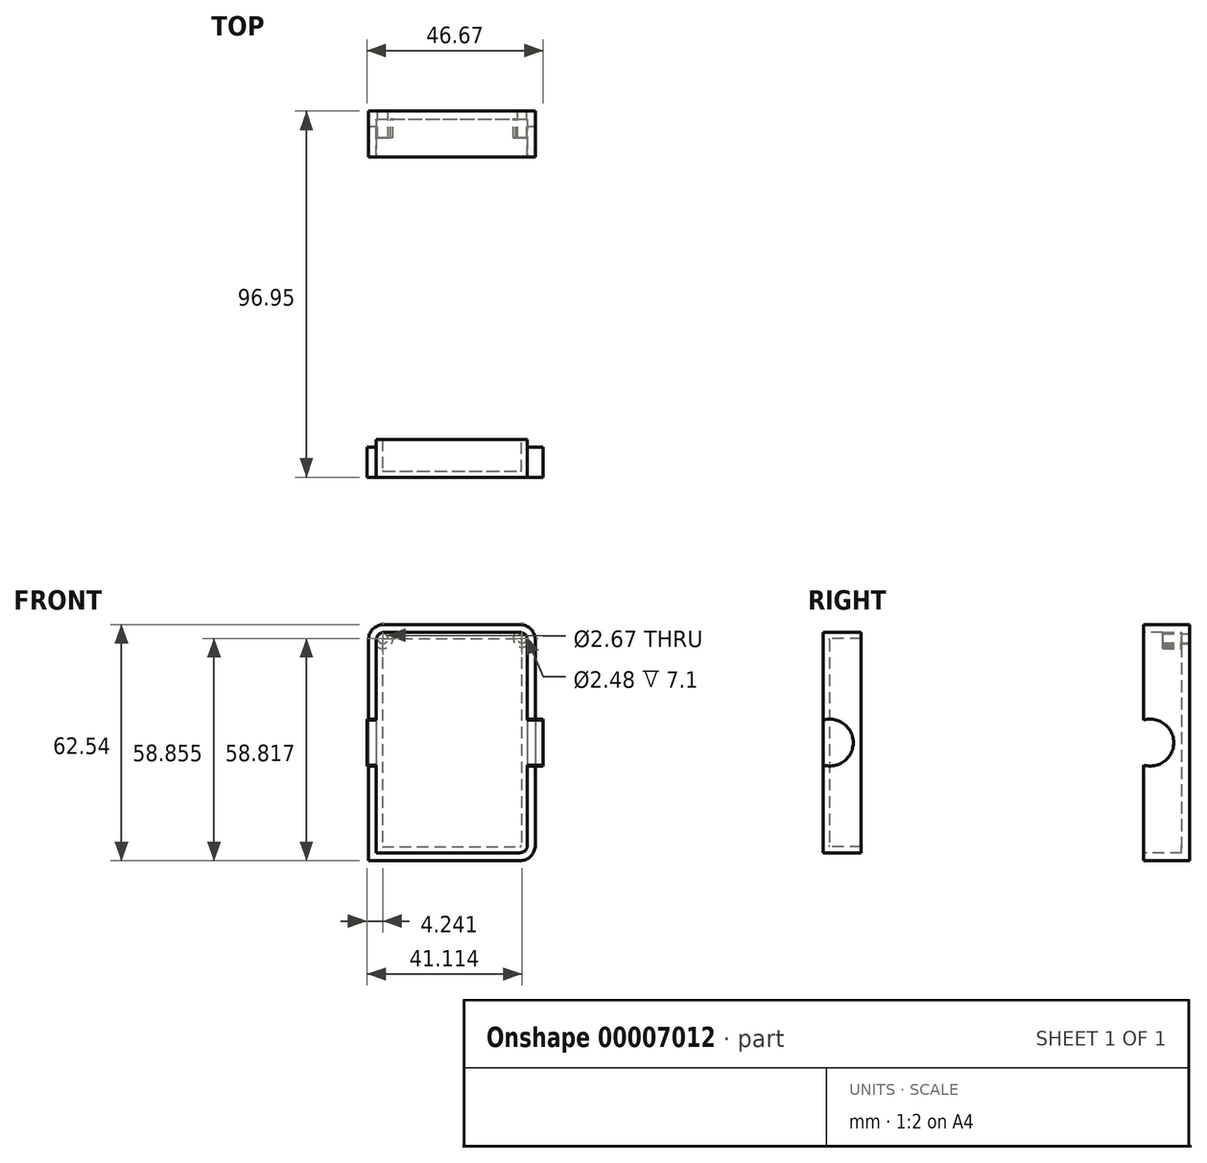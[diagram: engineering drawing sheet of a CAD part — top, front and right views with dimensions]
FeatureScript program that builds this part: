
annotation { "Feature Type Name" : "Feature", "Feature Type Description" : "" }
export const myFeature = defineFeature(function(context is Context, id is Id, definition is map)
    precondition{}
    {
        {
            var Q0;
            Q0=qCreatedBy(makeId("Front.planeOp"),FACE);
            var sketch = newSketch(context, id + "F0", { "sketchPlane" : qUnion([Q0])});
            skLineSegment(sketch, "E0.bottom", {"start": v(-18, 29.17) * mm, "end": v(18, 29.17) * mm});
            skLineSegment(sketch, "E0.top", {"start": v(-20, -29.17) * mm, "end": v(18, -29.17) * mm});
            skLineSegment(sketch, "E0.left", {"start": v(-20, 27.17) * mm, "end": v(-20, -29.17) * mm});
            skLineSegment(sketch, "E0.right", {"start": v(20, 27.17) * mm, "end": v(20, -27.17) * mm});
            skLineSegment(sketch, "E1", {"start": v(0, 39.19) * mm, "end": v(0, 29.17) * mm});
            skLineSegment(sketch, "E2", {"start": v(20, 0) * mm, "end": v(28.08, 0) * mm});
            skPoint(sketch, "E3.visualSharp", {"position": v(-20, 29.17) * mm});
            skArc(sketch, "E3.filletArc", {"start": v(-18, 29.17) * mm, "mid": v(-19.41, 28.58) * mm, "end": v(-20, 27.17) * mm});
            skPoint(sketch, "E4.visualSharp", {"position": v(20, 29.17) * mm});
            skArc(sketch, "E4.filletArc", {"start": v(20, 27.17) * mm, "mid": v(19.41, 28.58) * mm, "end": v(18, 29.17) * mm});
            skPoint(sketch, "E5.visualSharp", {"position": v(20, -29.17) * mm});
            skArc(sketch, "E5.filletArc", {"start": v(18, -29.17) * mm, "mid": v(19.41, -28.58) * mm, "end": v(20, -27.17) * mm});
            skSolve(sketch);
        }
        {
            var Q0;
            Q0=makeQuery(id+"F0.imprint","IMPRINT",FACE,{"disambiguationData":[TD([[makeQuery(id+"F0.imprint","IMPRINT",EDGE,{"derivedFrom":sQuery(id+"F0.wireOp",EDGE,"E0.bottom")}),-1.0]])]});
            extrude(context, id + "F1", {"entities" : qUnion([Q0]), "oppositeDirection" : true, "depth" : 10 * mm});
        }
        {
            var Q0;
            Q0=makeQuery(id+"F1.opExtrude","SWEPT_FACE",FACE,{"disambiguationData":[OSD([sQuery(id+"F0.wireOp",EDGE,"E0.left")])]});
            var sketch = newSketch(context, id + "F2", { "sketchPlane" : qUnion([Q0])});
            skCircle(sketch, "E6", {"center": v(-1.73, 0) * mm, "radius": 6.2 * mm});
            skSolve(sketch);
        }
        {
            var Q0;
            {var subQ0=makeQuery(id+"F1.opExtrude","CAP_EDGE",EDGE,{"disambiguationData":[OSD([sQuery(id+"F0.wireOp",EDGE,"E0.left")])],"isStart":true});var subQ1=sQuery(id+"F2.wireOp",EDGE,"E6");var subQ3=makeQuery(id+"F2.imprint","INTERSECT",VERTEX,{"disambiguationData":[OD(0.0)],"derivedFrom":[subQ0,subQ1]});Q0=makeQuery(id+"F2.imprint","IMPRINT",FACE,{"disambiguationData":[TD([[makeQuery(id+"F2.imprint","IMPRINT",EDGE,{"disambiguationData":[TD([[subQ3,1.0]])],"derivedFrom":subQ1}),1.0]])]});}
            extrude(context, id + "F3", {"entities" : qUnion([Q0]), "operationType" : NewBodyOperationType.ADD, "oppositeDirection" : true, "depth" : 44.16 * mm, "hasSecondDirection" : true, "secondDirectionOppositeDirection" : false, "secondDirectionDepth" : 2.5 * mm});
        }
        {
            var Q0;
            Q0=qCreatedBy(makeId("Right.planeOp"),FACE);
            var sketch = newSketch(context, id + "F4", { "sketchPlane" : qUnion([Q0])});
            skLineSegment(sketch, "E7", {"start": v(-6.91, 22.76) * mm, "end": v(-91.77, 22.76) * mm});
            skSolve(sketch);
        }
        {
            var Q0;
            Q0=makeQuery(id+"F1.opExtrude","SWEPT_BODY",BODY,{"disambiguationData":[OSD([sQuery(id+"F0.wireOp",EDGE,"E0.bottom"),sQuery(id+"F0.wireOp",EDGE,"E0.top"),sQuery(id+"F0.wireOp",EDGE,"E0.left"),sQuery(id+"F0.wireOp",EDGE,"E0.right")])]});
            var Q1;
            Q1=sQuery(id+"F4.wireOp",EDGE,"E7");
            transform(context, id + "F5", {"entities" : qUnion([Q0]), "transformType" : TransformType.TRANSLATION_ENTITY, "oppositeDirectionEntity" : false, "transformLine" : qUnion([Q1]), "makeCopy" : true});
        }
        {
            var Q0;
            {var subQ0=sQuery(id+"F0.wireOp",EDGE,"E0.left");Q0=makeQuery(id+"F3.boolean.opBoolean","MERGE",FACE,{"derivedFrom":[makeQuery(id+"F1.opExtrude","CAP_FACE",FACE,{"disambiguationData":[OSD([sQuery(id+"F0.wireOp",EDGE,"E0.bottom"),sQuery(id+"F0.wireOp",EDGE,"E0.top"),subQ0,sQuery(id+"F0.wireOp",EDGE,"E0.right")])],"isStart":true}),makeQuery(id+"F3.opExtrude","SWEPT_FACE",FACE,{"disambiguationData":[OSD([subQ0])]})]});}
            var Q1;
            Q1=makeQuery(id+"F3.opExtrude","CAP_FACE",FACE,{"disambiguationData":[OSD([sQuery(id+"F0.wireOp",EDGE,"E0.left"),sQuery(id+"F2.wireOp",EDGE,"E6")])],"isStart":true});
            var Q2;
            Q2=makeQuery(id+"F3.opExtrude","CAP_FACE",FACE,{"disambiguationData":[OSD([sQuery(id+"F0.wireOp",EDGE,"E0.left"),sQuery(id+"F2.wireOp",EDGE,"E6")])],"isStart":false});
            var Q3;
            Q3=makeQuery(id+"F3.opExtrude","SWEPT_FACE",FACE,{"disambiguationData":[OSD([sQuery(id+"F2.wireOp",EDGE,"E6")])]});
            shell(context, id + "F6", {"entities" : qUnion([Q0, Q1, Q2, Q3]), "thickness" : 2.1 * mm, "oppositeDirection" : true});
        }
        {
            var Q0;
            Q0=makeQuery(id+"F5.opPattern","COPY",FACE,{"derivedFrom":makeQuery(id+"F1.opExtrude","CAP_FACE",FACE,{"disambiguationData":[OSD([sQuery(id+"F0.wireOp",EDGE,"E0.bottom"),sQuery(id+"F0.wireOp",EDGE,"E0.top"),sQuery(id+"F0.wireOp",EDGE,"E0.left"),sQuery(id+"F0.wireOp",EDGE,"E0.right")])],"isStart":false}),"instanceName":"1"});
            shell(context, id + "F7", {"entities" : qUnion([Q0]), "thickness" : 1.6 * mm});
        }
        {
            var Q0;
            {var subQ0=sQuery(id+"F0.wireOp",EDGE,"E0.left");var subQ1=sQuery(id+"F2.wireOp",EDGE,"E6");Q0=makeQuery(id+"F7.opShell","OFFSET_FACE",FACE,{"disambiguationData":[OSD([subQ0,subQ1]),TDD([makeQuery(id+"F5.opPattern","COPY",FACE,{"derivedFrom":makeQuery(id+"F3.opExtrude","CAP_FACE",FACE,{"disambiguationData":[OSD([subQ0,subQ1])],"isStart":false}),"instanceName":"1"})])]});}
            var Q1;
            Q1=makeQuery(id+"F7.opShell","OFFSET_FACE",FACE,{"disambiguationData":[OSD([sQuery(id+"F0.wireOp",EDGE,"E0.right")])]});
            extrude(context, id + "F8", {"entities" : qUnion([Q0]), "operationType" : NewBodyOperationType.ADD, "endBound" : BoundingType.UP_TO_SURFACE, "endBoundEntityFace" : qUnion([Q1]), "depth" : 4.2 * mm});
        }
        {
            var Q0;
            {var subQ0=sQuery(id+"F0.wireOp",EDGE,"E0.left");var subQ1=sQuery(id+"F2.wireOp",EDGE,"E6");Q0=makeQuery(id+"F7.opShell","OFFSET_FACE",FACE,{"disambiguationData":[OSD([subQ0,subQ1]),TDD([makeQuery(id+"F5.opPattern","COPY",FACE,{"derivedFrom":makeQuery(id+"F3.opExtrude","CAP_FACE",FACE,{"disambiguationData":[OSD([subQ0,subQ1])],"isStart":true}),"instanceName":"1"})])]});}
            var Q1;
            Q1=makeQuery(id+"F7.opShell","OFFSET_FACE",FACE,{"disambiguationData":[OSD([sQuery(id+"F0.wireOp",EDGE,"E0.left")])]});
            extrude(context, id + "F9", {"entities" : qUnion([Q0]), "operationType" : NewBodyOperationType.ADD, "endBound" : BoundingType.UP_TO_SURFACE, "endBoundEntityFace" : qUnion([Q1]), "depth" : 25 * mm});
        }
        {
            var Q0;
            Q0=makeQuery(id+"F6.opShell","OFFSET_FACE",FACE,{"disambiguationData":[OSD([sQuery(id+"F0.wireOp",EDGE,"E0.bottom"),sQuery(id+"F0.wireOp",EDGE,"E0.top"),sQuery(id+"F0.wireOp",EDGE,"E0.left"),sQuery(id+"F0.wireOp",EDGE,"E0.right")])]});
            var sketch = newSketch(context, id + "F10", { "sketchPlane" : qUnion([Q0])});
            skCircle(sketch, "E8", {"center": v(-18.27, 27.55) * mm, "radius": 1.34 * mm});
            skCircle(sketch, "E9", {"center": v(-18.27, 27.55) * mm, "radius": 2.64 * mm});
            skCircle(sketch, "E10", {"center": v(18.6, 27.59) * mm, "radius": 1.24 * mm});
            skCircle(sketch, "E11", {"center": v(18.6, 27.59) * mm, "radius": 2.32 * mm});
            skSolve(sketch);
        }
        {
            var Q0;
            Q0=makeQuery(id+"F10.imprint","IMPRINT",FACE,{"disambiguationData":[TD([[makeQuery(id+"F10.imprint","IMPRINT",EDGE,{"derivedFrom":sQuery(id+"F10.wireOp",EDGE,"E8")}),-1.0]])]});
            var Q1;
            Q1=makeQuery(id+"F10.imprint","IMPRINT",FACE,{"disambiguationData":[TD([[makeQuery(id+"F10.imprint","IMPRINT",EDGE,{"derivedFrom":sQuery(id+"F10.wireOp",EDGE,"E10")}),-1.0]])]});
            extrude(context, id + "F11", {"entities" : qUnion([Q0, Q1]), "operationType" : NewBodyOperationType.ADD, "depth" : 5 * mm});
        }
        {
            var Q0;
            Q0=makeQuery(id+"F10.imprint","IMPRINT",FACE,{"disambiguationData":[TD([[makeQuery(id+"F10.imprint","IMPRINT",EDGE,{"derivedFrom":sQuery(id+"F10.wireOp",EDGE,"E8")}),1.0]])]});
            var Q1;
            Q1=makeQuery(id+"F10.imprint","IMPRINT",FACE,{"disambiguationData":[TD([[makeQuery(id+"F10.imprint","IMPRINT",EDGE,{"derivedFrom":sQuery(id+"F10.wireOp",EDGE,"E10")}),1.0]])]});
            extrude(context, id + "F12", {"entities" : qUnion([Q0, Q1]), "operationType" : NewBodyOperationType.REMOVE, "oppositeDirection" : true, "depth" : 25 * mm});
        }
    });
